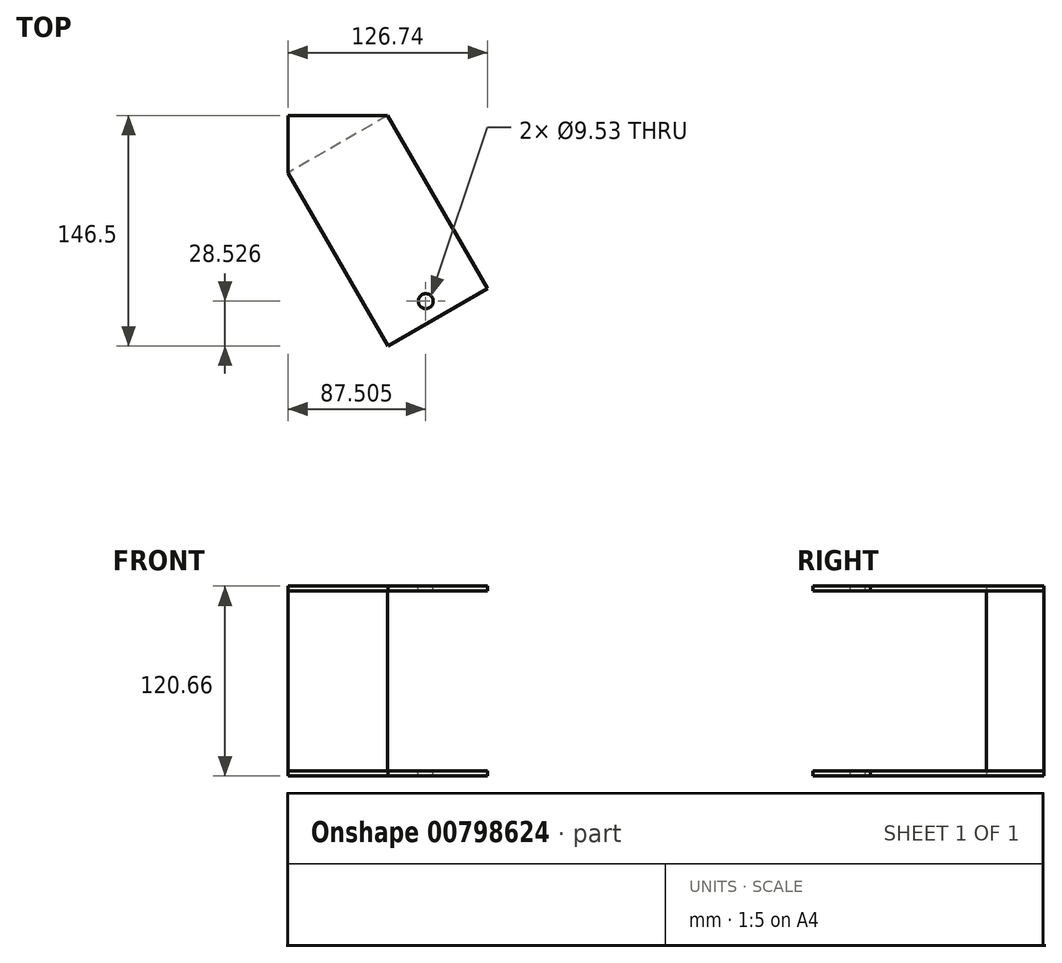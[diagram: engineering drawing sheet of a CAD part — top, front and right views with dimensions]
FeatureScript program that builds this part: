
annotation { "Feature Type Name" : "Feature", "Feature Type Description" : "" }
export const myFeature = defineFeature(function(context is Context, id is Id, definition is map)
    precondition{}
    {
        {
            var Q0;
            Q0=qCreatedBy(makeId("Top.planeOp"),FACE);
            var sketch = newSketch(context, id + "F0", { "sketchPlane" : qUnion([Q0])});
            skLineSegment(sketch, "E0", {"start": v(0, 0) * mm, "end": v(63.24, 0) * mm});
            skLineSegment(sketch, "E1", {"start": v(63.24, 0) * mm, "end": v(0, -36.51) * mm});
            skLineSegment(sketch, "E2", {"start": v(0, -36.51) * mm, "end": v(0, 0) * mm});
            skSolve(sketch);
        }
        {
            var Q0;
            Q0 = qSketchRegion(id + "F0", true);
            extrude(context, id + "F1", {"entities" : qUnion([Q0]), "endBound" : BoundingType.SYMMETRIC, "depth" : 120.65 * mm, "offsetDistance" : 25.4 * mm});
        }
        {
            var Q0;
            Q0=makeQuery(id+"F1.opExtrude","CAP_FACE",FACE,{"disambiguationData":[OSD([sQuery(id+"F0.wireOp",EDGE,"E0"),sQuery(id+"F0.wireOp",EDGE,"E1"),sQuery(id+"F0.wireOp",EDGE,"E2")])],"isStart":false});
            var sketch = newSketch(context, id + "F2", { "sketchPlane" : qUnion([Q0])});
            skLineSegment(sketch, "E3", {"start": v(0, -36.51) * mm, "end": v(63.5, -146.5) * mm});
            skLineSegment(sketch, "E4", {"start": v(63.5, -146.5) * mm, "end": v(126.74, -109.99) * mm});
            skLineSegment(sketch, "E5", {"start": v(126.74, -109.99) * mm, "end": v(63.24, 0) * mm});
            skLineSegment(sketch, "E6", {"start": v(63.24, 0) * mm, "end": v(0, -36.51) * mm});
            skSolve(sketch);
        }
        {
            var Q0;
            Q0 = qSketchRegion(id + "F2", true);
            extrude(context, id + "F3", {"entities" : qUnion([Q0]), "operationType" : NewBodyOperationType.ADD, "oppositeDirection" : true, "depth" : 3.17 * mm, "offsetDistance" : 25.4 * mm});
        }
        {
            var Q0;
            Q0=makeQuery(id+"F1.opExtrude","CAP_FACE",FACE,{"disambiguationData":[OSD([sQuery(id+"F0.wireOp",EDGE,"E0"),sQuery(id+"F0.wireOp",EDGE,"E1"),sQuery(id+"F0.wireOp",EDGE,"E2")])],"isStart":true});
            var sketch = newSketch(context, id + "F4", { "sketchPlane" : qUnion([Q0])});
            skLineSegment(sketch, "E7", {"start": v(0, 36.51) * mm, "end": v(63.5, 146.5) * mm});
            skLineSegment(sketch, "E8", {"start": v(63.5, 146.5) * mm, "end": v(126.74, 109.99) * mm});
            skLineSegment(sketch, "E9", {"start": v(126.74, 109.99) * mm, "end": v(63.24, 0) * mm});
            skLineSegment(sketch, "E10", {"start": v(63.24, 0) * mm, "end": v(0, 36.51) * mm});
            skSolve(sketch);
        }
        {
            var Q0;
            Q0 = qSketchRegion(id + "F4", true);
            extrude(context, id + "F5", {"entities" : qUnion([Q0]), "operationType" : NewBodyOperationType.ADD, "oppositeDirection" : true, "depth" : 3.17 * mm, "offsetDistance" : 25.4 * mm});
        }
        {
            var Q0;
            Q0=makeQuery(id+"F3.boolean.opBoolean","MERGE",FACE,{"derivedFrom":[makeQuery(id+"F1.opExtrude","CAP_FACE",FACE,{"disambiguationData":[OSD([sQuery(id+"F0.wireOp",EDGE,"E0"),sQuery(id+"F0.wireOp",EDGE,"E1"),sQuery(id+"F0.wireOp",EDGE,"E2")])],"isStart":false}),makeQuery(id+"F3.opExtrude","CAP_FACE",FACE,{"disambiguationData":[OSD([sQuery(id+"F2.wireOp",EDGE,"E3"),sQuery(id+"F2.wireOp",EDGE,"E4"),sQuery(id+"F2.wireOp",EDGE,"E5"),sQuery(id+"F2.wireOp",EDGE,"E6")])],"isStart":true})]});
            var sketch = newSketch(context, id + "F6", { "sketchPlane" : qUnion([Q0])});
            skLineSegment(sketch, "E11", {"start": v(0, 0) * mm, "end": v(95.12, -128.24) * mm, "construction": true});
            skCircle(sketch, "E12", {"center": v(87.5, -117.97) * mm, "radius": 4.76 * mm});
            skLineSegment(sketch, "E13", {"start": v(0, -36.51) * mm, "end": v(63.24, 0) * mm, "construction": true});
            skSolve(sketch);
        }
        {
            var Q0;
            Q0 = qSketchRegion(id + "F6", true);
            extrude(context, id + "F7", {"entities" : qUnion([Q0]), "operationType" : NewBodyOperationType.REMOVE, "endBound" : BoundingType.THROUGH_ALL, "oppositeDirection" : true, "depth" : 25.4 * mm, "offsetDistance" : 25.4 * mm});
        }
    });
